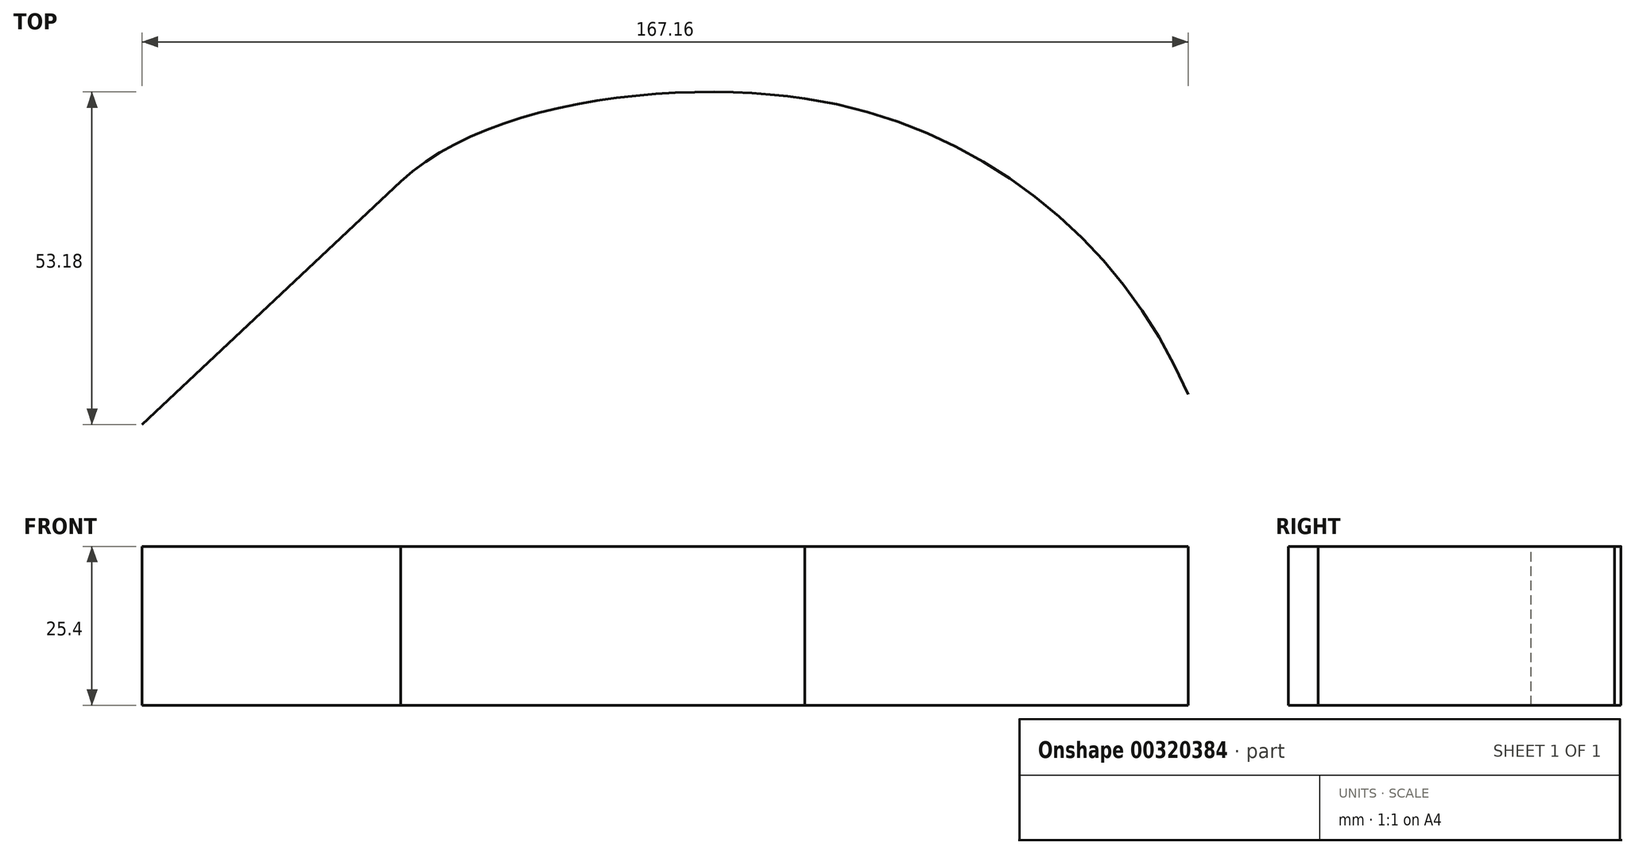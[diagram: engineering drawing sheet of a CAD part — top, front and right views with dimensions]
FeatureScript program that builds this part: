
annotation { "Feature Type Name" : "Feature", "Feature Type Description" : "" }
export const myFeature = defineFeature(function(context is Context, id is Id, definition is map)
    precondition{}
    {
        {
            var Q0;
            Q0=qCreatedBy(makeId("Top.planeOp"),FACE);
            var sketch = newSketch(context, id + "F0", { "sketchPlane" : qUnion([Q0])});
            skLineSegment(sketch, "E0", {"start": v(-70.88, 7.14) * mm, "end": v(-29.55, 45.98) * mm});
            skArc(sketch, "E1", {"start": v(96.28, 11.95) * mm, "mid": v(71.81, 43.58) * mm, "end": v(35.03, 59.26) * mm});
            skSolve(sketch);
        }
        {
            var Q0;
            Q0=sQuery(id+"F0.wireOp",EDGE,"E0");
            var Q1;
            Q1=sQuery(id+"F0.wireOp",EDGE,"E1");
            extrude(context, id + "F1", {"bodyType" : ToolBodyType.SURFACE, "surfaceEntities" : qUnion([Q0, Q1]), "depth" : 25.4 * mm});
        }
        {
            var Q0;
            Q0=makeQuery(id+"F1.opExtrude","SWEPT_EDGE",EDGE,{"disambiguationData":[OSD([sQuery(id+"F0.wireOp",VERTEX,"E0.end")])]});
            var Q1;
            Q1=makeQuery(id+"F1.opExtrude","SWEPT_EDGE",EDGE,{"disambiguationData":[OSD([sQuery(id+"F0.wireOp",VERTEX,"E1.end")])]});
            loft(context, id + "F2", {"bodyType" : ToolBodyType.SURFACE, "startCondition" : LoftEndDerivativeType.MATCH_TANGENT, "startMagnitude" : 1, "endCondition" : LoftEndDerivativeType.MATCH_TANGENT, "endMagnitude" : 1, "wireProfilesArray" : [{ "wireProfileEntities" : qUnion([Q0]) }, { "wireProfileEntities" : qUnion([Q1]) }]});
        }
        {
            var Q0;
            Q0=makeQuery(id+"F1.opExtrude","SWEPT_EDGE",EDGE,{"disambiguationData":[OSD([sQuery(id+"F0.wireOp",VERTEX,"E1.start")])]});
            var Q1;
            Q1=makeQuery(id+"F1.opExtrude","CAP_VERTEX",VERTEX,{"disambiguationData":[OSD([sQuery(id+"F0.wireOp",VERTEX,"E1.start")])],"isStart":false});
            cPlane(context, id + "F3", {"entities" : qUnion([Q0, Q1]), "cplaneType" : CPlaneType.LINE_POINT, "offset" : 25.4 * mm, "width" : 152.4 * mm, "height" : 152.4 * mm});
        }
    });
